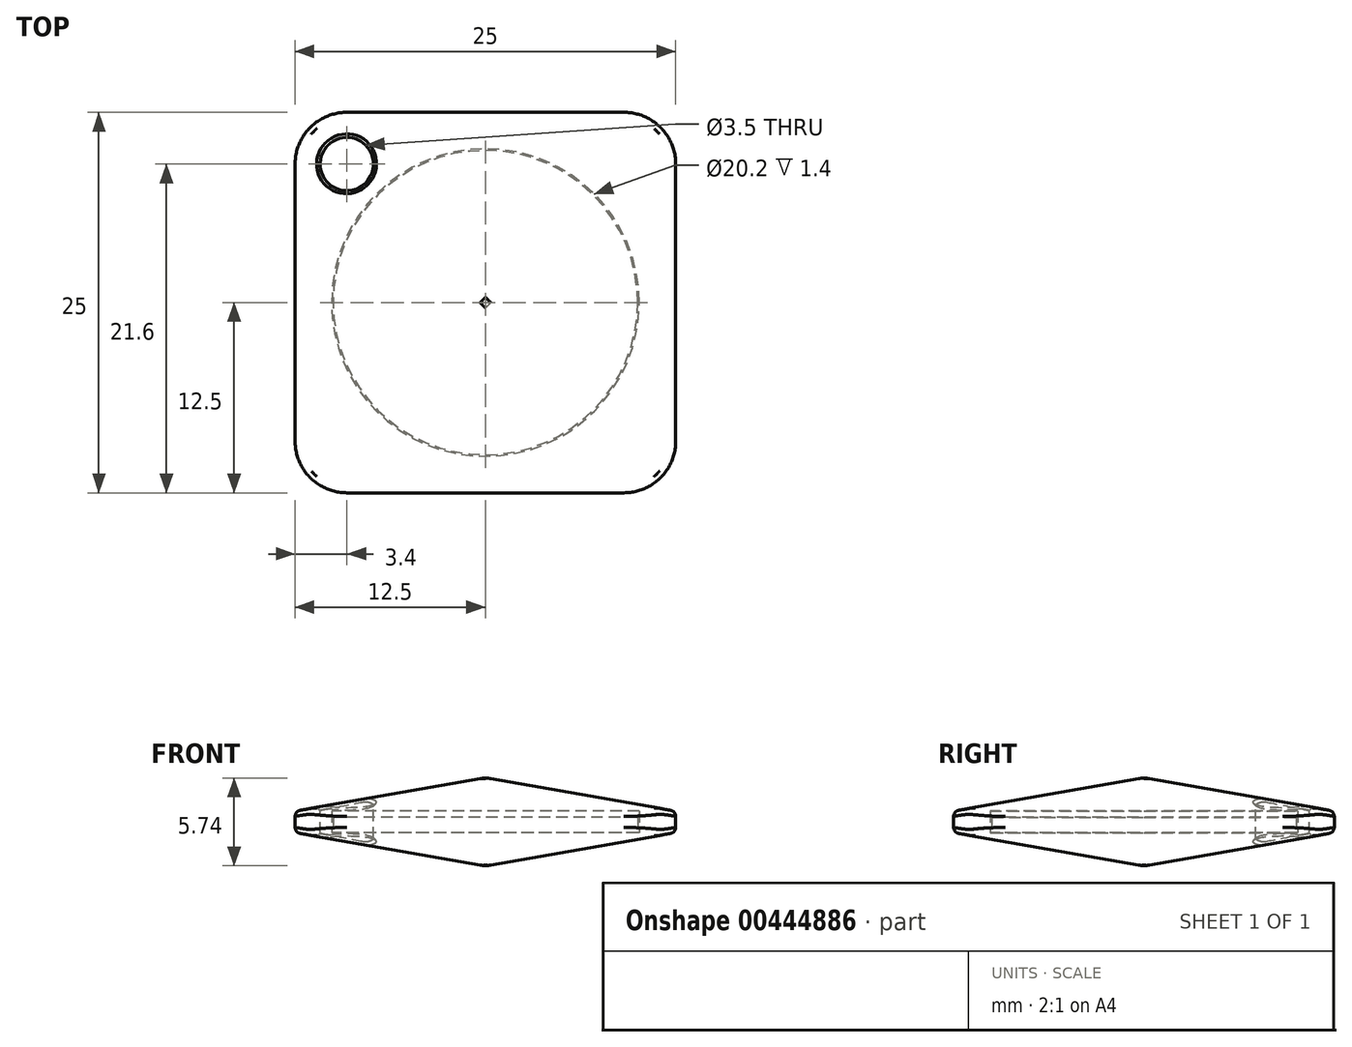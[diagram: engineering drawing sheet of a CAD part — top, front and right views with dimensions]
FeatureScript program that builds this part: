
annotation { "Feature Type Name" : "Feature", "Feature Type Description" : "" }
export const myFeature = defineFeature(function(context is Context, id is Id, definition is map)
    precondition{}
    {
        {
            var Q0;
            Q0=qCreatedBy(makeId("Top.planeOp"),FACE);
            var sketch = newSketch(context, id + "F0", { "sketchPlane" : qUnion([Q0])});
            skCircle(sketch, "E0", {"center": v(0, 0) * mm, "radius": 10 * mm});
            skSolve(sketch);
        }
        {
            var Q0;
            Q0 = qSketchRegion(id + "F0", true);
            extrude(context, id + "F1", {"entities" : qUnion([Q0]), "depth" : 1 * mm});
        }
        {
            var Q0;
            Q0=qCreatedBy(makeId("Top.planeOp"),FACE);
            var sketch = newSketch(context, id + "F2", { "sketchPlane" : qUnion([Q0])});
            skLineSegment(sketch, "E1.bottom", {"start": v(12.5, 12.5) * mm, "end": v(-12.5, 12.5) * mm});
            skLineSegment(sketch, "E1.top", {"start": v(12.5, -12.5) * mm, "end": v(-12.5, -12.5) * mm});
            skLineSegment(sketch, "E1.left", {"start": v(12.5, 12.5) * mm, "end": v(12.5, -12.5) * mm});
            skLineSegment(sketch, "E1.right", {"start": v(-12.5, 12.5) * mm, "end": v(-12.5, -12.5) * mm});
            skPoint(sketch, "E1.middle", {"position": v(0, 0) * mm});
            skSolve(sketch);
        }
        {
            var Q0;
            Q0 = qSketchRegion(id + "F2", true);
            extrude(context, id + "F3", {"entities" : qUnion([Q0]), "oppositeDirection" : true, "depth" : 10 * mm, "hasDraft" : true, "draftAngle" : 80 * degree, "draftPullDirection" : true});
        }
        {
            var Q0;
            Q0=makeQuery(id+"F3.opExtrude","CAP_FACE",FACE,{"disambiguationData":[OSD([sQuery(id+"F2.wireOp",EDGE,"E1.bottom"),sQuery(id+"F2.wireOp",EDGE,"E1.top"),sQuery(id+"F2.wireOp",EDGE,"E1.left"),sQuery(id+"F2.wireOp",EDGE,"E1.right")])],"isStart":true});
            var sketch = newSketch(context, id + "F4", { "sketchPlane" : qUnion([Q0])});
            skLineSegment(sketch, "E2.0.0", {"start": v(12.5, -12.5) * mm, "end": v(-12.5, -12.5) * mm});
            skLineSegment(sketch, "E2.0.1", {"start": v(12.5, 12.5) * mm, "end": v(12.5, -12.5) * mm});
            skLineSegment(sketch, "E2.0.2", {"start": v(12.5, 12.5) * mm, "end": v(-12.5, 12.5) * mm});
            skLineSegment(sketch, "E2.0.3", {"start": v(-12.5, 12.5) * mm, "end": v(-12.5, -12.5) * mm});
            skCircle(sketch, "E3", {"center": v(0, 0) * mm, "radius": 10.1 * mm});
            skSolve(sketch);
        }
        {
            var Q0;
            Q0 = qSketchRegion(id + "F4", true);
            extrude(context, id + "F5", {"entities" : qUnion([Q0]), "operationType" : NewBodyOperationType.ADD, "depth" : 1.4 * mm});
        }
        {
            var Q0;
            Q0=makeQuery(id+"F5.opExtrude","CAP_FACE",FACE,{"disambiguationData":[OSD([sQuery(id+"F4.wireOp",EDGE,"E2.0.0"),sQuery(id+"F4.wireOp",EDGE,"E2.0.1"),sQuery(id+"F4.wireOp",EDGE,"E2.0.2"),sQuery(id+"F4.wireOp",EDGE,"E2.0.3"),sQuery(id+"F4.wireOp",EDGE,"E3")])],"isStart":false});
            var sketch = newSketch(context, id + "F6", { "sketchPlane" : qUnion([Q0])});
            skLineSegment(sketch, "E4.0.0", {"start": v(12.5, -12.5) * mm, "end": v(-12.5, -12.5) * mm});
            skLineSegment(sketch, "E4.0.1", {"start": v(12.5, 12.5) * mm, "end": v(12.5, -12.5) * mm});
            skLineSegment(sketch, "E4.0.2", {"start": v(12.5, 12.5) * mm, "end": v(-12.5, 12.5) * mm});
            skLineSegment(sketch, "E4.0.3", {"start": v(-12.5, 12.5) * mm, "end": v(-12.5, -12.5) * mm});
            skSolve(sketch);
        }
        {
            var Q0;
            Q0=makeQuery(id+"F6.imprint","IMPRINT",FACE,{"disambiguationData":[TD([[makeQuery(id+"F6.imprint","IMPRINT",EDGE,{"derivedFrom":sQuery(id+"F6.wireOp",EDGE,"E4.0.0")}),-1.0]])]});
            var Q1;
            Q1=makeQuery(id+"F6.imprint","IMPRINT",FACE,{"disambiguationData":[TD([[makeQuery(id+"F6.imprint","IMPRINT",EDGE,{"derivedFrom":makeQuery(id+"F5.opExtrude","CAP_EDGE",EDGE,{"disambiguationData":[OSD([sQuery(id+"F4.wireOp",EDGE,"E3")])],"isStart":false})}),1.0]])]});
            extrude(context, id + "F7", {"entities" : qUnion([Q0, Q1]), "operationType" : NewBodyOperationType.ADD, "depth" : 25 * mm, "hasDraft" : true, "draftAngle" : 80 * degree, "draftPullDirection" : true});
        }
        {
            var Q0;
            Q0=makeQuery(id+"F5.opExtrude","SWEPT_EDGE",EDGE,{"disambiguationData":[OSD([sQuery(id+"F4.wireOp",EDGE,"E2.0.0"),sQuery(id+"F4.wireOp",EDGE,"E2.0.3")])]});
            var Q1;
            Q1=makeQuery(id+"F5.opExtrude","SWEPT_EDGE",EDGE,{"disambiguationData":[OSD([sQuery(id+"F4.wireOp",EDGE,"E2.0.2"),sQuery(id+"F4.wireOp",EDGE,"E2.0.3")])]});
            var Q2;
            Q2=makeQuery(id+"F5.opExtrude","SWEPT_EDGE",EDGE,{"disambiguationData":[OSD([sQuery(id+"F4.wireOp",EDGE,"E2.0.0"),sQuery(id+"F4.wireOp",EDGE,"E2.0.1")])]});
            var Q3;
            Q3=makeQuery(id+"F5.opExtrude","SWEPT_EDGE",EDGE,{"disambiguationData":[OSD([sQuery(id+"F4.wireOp",EDGE,"E2.0.1"),sQuery(id+"F4.wireOp",EDGE,"E2.0.2")])]});
            fillet(context, id + "F8", {"entities" : qUnion([Q0, Q1, Q2, Q3]), "radius" : 3.4 * mm, "tangentPropagation" : true, "allowEdgeOverflow" : false});
        }
        {
            var Q0;
            Q0=qCreatedBy(makeId("Top.planeOp"),FACE);
            var sketch = newSketch(context, id + "F9", { "sketchPlane" : qUnion([Q0])});
            skArc(sketch, "E5.0", {"start": v(-9.1, 12.5) * mm, "mid": v(-10.4, 12.24) * mm, "end": v(-11.5, 11.5) * mm});
            skCircle(sketch, "E6", {"center": v(-9.1, 9.1) * mm, "radius": 1.75 * mm});
            skSolve(sketch);
        }
        {
            var Q0;
            Q0 = qSketchRegion(id + "F9", true);
            extrude(context, id + "F10", {"entities" : qUnion([Q0]), "operationType" : NewBodyOperationType.REMOVE, "oppositeDirection" : true, "depth" : 25 * mm, "hasSecondDirection" : true, "secondDirectionOppositeDirection" : false, "secondDirectionDepth" : 25 * mm});
        }
        {
            var Q0;
            {var subQ0=sQuery(id+"F6.wireOp",EDGE,"E4.0.2");var subQ1=sQuery(id+"F6.wireOp",EDGE,"E4.0.3");Q0=makeQuery(id+"F10.boolean.opBoolean","SPLIT",EDGE,{"disambiguationData":[TD([makeQuery(id+"F7.opExtrude","SWEPT_FACE",FACE,{"disambiguationData":[OSD([sQuery(id+"F6.wireOp",EDGE,"E4.0.0")])]})])],"derivedFrom":makeQuery(id+"F7.opExtrude","SWEPT_EDGE",EDGE,{"disambiguationData":[OSD([subQ0,subQ1])]})});}
            var Q1;
            {var subQ0=sQuery(id+"F6.wireOp",EDGE,"E4.0.2");var subQ1=sQuery(id+"F6.wireOp",EDGE,"E4.0.3");Q1=makeQuery(id+"F10.boolean.opBoolean","SPLIT",EDGE,{"disambiguationData":[TD([makeQuery(id+"F8.opFillet","BLEND_FACE",FACE,{"disambiguationData":[OSD([sQuery(id+"F4.wireOp",EDGE,"E2.0.2"),sQuery(id+"F4.wireOp",EDGE,"E2.0.3")])]})])],"derivedFrom":makeQuery(id+"F7.opExtrude","SWEPT_EDGE",EDGE,{"disambiguationData":[OSD([subQ0,subQ1])]})});}
            var Q2;
            Q2=makeQuery(id+"F7.opExtrude","SWEPT_EDGE",EDGE,{"disambiguationData":[OSD([sQuery(id+"F6.wireOp",EDGE,"E4.0.1"),sQuery(id+"F6.wireOp",EDGE,"E4.0.2")])]});
            var Q3;
            Q3=makeQuery(id+"F7.opExtrude","SWEPT_EDGE",EDGE,{"disambiguationData":[OSD([sQuery(id+"F6.wireOp",EDGE,"E4.0.0"),sQuery(id+"F6.wireOp",EDGE,"E4.0.1")])]});
            var Q4;
            Q4=makeQuery(id+"F7.opExtrude","SWEPT_EDGE",EDGE,{"disambiguationData":[OSD([sQuery(id+"F6.wireOp",EDGE,"E4.0.0"),sQuery(id+"F6.wireOp",EDGE,"E4.0.3")])]});
            var Q5;
            {var subQ0=sQuery(id+"F2.wireOp",EDGE,"E1.right");var subQ1=sQuery(id+"F2.wireOp",EDGE,"E1.bottom");Q5=makeQuery(id+"F10.boolean.opBoolean","SPLIT",EDGE,{"disambiguationData":[TD([makeQuery(id+"F3.opExtrude","SWEPT_FACE",FACE,{"disambiguationData":[OSD([sQuery(id+"F2.wireOp",EDGE,"E1.top")])]})])],"derivedFrom":makeQuery(id+"F3.opExtrude","SWEPT_EDGE",EDGE,{"disambiguationData":[OSD([subQ1,subQ0])]})});}
            var Q6;
            Q6=makeQuery(id+"F3.opExtrude","SWEPT_EDGE",EDGE,{"disambiguationData":[OSD([sQuery(id+"F2.wireOp",EDGE,"E1.bottom"),sQuery(id+"F2.wireOp",EDGE,"E1.left")])]});
            var Q7;
            Q7=makeQuery(id+"F3.opExtrude","SWEPT_EDGE",EDGE,{"disambiguationData":[OSD([sQuery(id+"F2.wireOp",EDGE,"E1.top"),sQuery(id+"F2.wireOp",EDGE,"E1.left")])]});
            var Q8;
            Q8=makeQuery(id+"F3.opExtrude","SWEPT_EDGE",EDGE,{"disambiguationData":[OSD([sQuery(id+"F2.wireOp",EDGE,"E1.top"),sQuery(id+"F2.wireOp",EDGE,"E1.right")])]});
            var Q9;
            {var subQ0=sQuery(id+"F2.wireOp",EDGE,"E1.bottom");var subQ1=sQuery(id+"F2.wireOp",EDGE,"E1.right");Q9=makeQuery(id+"F10.boolean.opBoolean","SPLIT",EDGE,{"disambiguationData":[TD([makeQuery(id+"F8.opFillet","BLEND_FACE",FACE,{"disambiguationData":[OSD([sQuery(id+"F4.wireOp",EDGE,"E2.0.2"),sQuery(id+"F4.wireOp",EDGE,"E2.0.3")])]})])],"derivedFrom":makeQuery(id+"F3.opExtrude","SWEPT_EDGE",EDGE,{"disambiguationData":[OSD([subQ0,subQ1])]})});}
            fillet(context, id + "F11", {"entities" : qUnion([Q0, Q1, Q2, Q3, Q4, Q5, Q6, Q7, Q8, Q9]), "radius" : 2 * mm, "tangentPropagation" : true, "allowEdgeOverflow" : false});
        }
        {
            var Q0;
            Q0=makeQuery(id+"F5.boolean.opBoolean","MERGE",EDGE,{"derivedFrom":[makeQuery(id+"F3.opExtrude","CAP_EDGE",EDGE,{"disambiguationData":[OSD([sQuery(id+"F2.wireOp",EDGE,"E1.left")])],"isStart":true}),makeQuery(id+"F5.opExtrude","CAP_EDGE",EDGE,{"disambiguationData":[OSD([sQuery(id+"F4.wireOp",EDGE,"E2.0.1")])],"isStart":true})]});
            var Q1;
            Q1=makeQuery(id+"F7.boolean.opBoolean","MERGE",EDGE,{"derivedFrom":[makeQuery(id+"F5.opExtrude","CAP_EDGE",EDGE,{"disambiguationData":[OSD([sQuery(id+"F4.wireOp",EDGE,"E2.0.0")])],"isStart":false}),makeQuery(id+"F7.opExtrude","CAP_EDGE",EDGE,{"disambiguationData":[OSD([sQuery(id+"F6.wireOp",EDGE,"E4.0.0")])],"isStart":true})]});
            fillet(context, id + "F12", {"entities" : qUnion([Q0, Q1]), "radius" : 0.4 * mm, "tangentPropagation" : true, "allowEdgeOverflow" : false});
        }
        {
            var Q0;
            Q0=makeQuery(id+"F10.boolean.opBoolean","INTERSECT",EDGE,{"derivedFrom":[makeQuery(id+"F7.opExtrude","SWEPT_FACE",FACE,{"disambiguationData":[OSD([sQuery(id+"F6.wireOp",EDGE,"E4.0.2")])]}),makeQuery(id+"F10.opExtrude","SWEPT_FACE",FACE,{"disambiguationData":[OSD([sQuery(id+"F9.wireOp",EDGE,"E6")])]})]});
            var Q1;
            Q1=makeQuery(id+"F10.boolean.opBoolean","INTERSECT",EDGE,{"derivedFrom":[makeQuery(id+"F7.opExtrude","SWEPT_FACE",FACE,{"disambiguationData":[OSD([sQuery(id+"F6.wireOp",EDGE,"E4.0.3")])]}),makeQuery(id+"F10.opExtrude","SWEPT_FACE",FACE,{"disambiguationData":[OSD([sQuery(id+"F9.wireOp",EDGE,"E6")])]})]});
            var Q2;
            Q2=makeQuery(id+"F10.boolean.opBoolean","INTERSECT",EDGE,{"derivedFrom":[makeQuery(id+"F3.opExtrude","SWEPT_FACE",FACE,{"disambiguationData":[OSD([sQuery(id+"F2.wireOp",EDGE,"E1.bottom")])]}),makeQuery(id+"F10.opExtrude","SWEPT_FACE",FACE,{"disambiguationData":[OSD([sQuery(id+"F9.wireOp",EDGE,"E6")])]})]});
            chamfer(context, id + "F13", {"entities" : qUnion([Q0, Q1, Q2]), "width" : 0.2 * mm, "tangentPropagation" : true});
        }
    });
